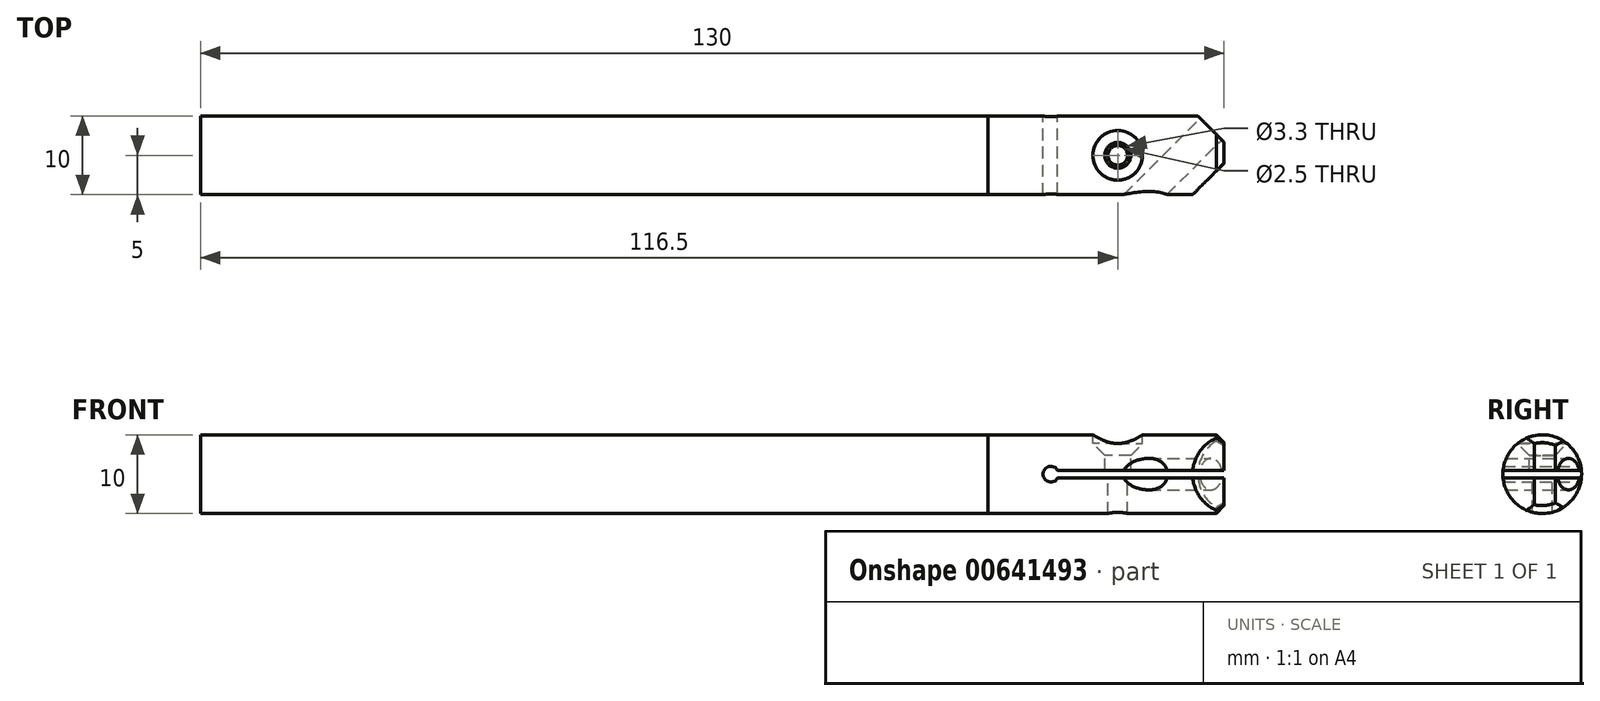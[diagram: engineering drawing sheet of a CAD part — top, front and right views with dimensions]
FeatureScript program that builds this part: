
annotation { "Feature Type Name" : "Feature", "Feature Type Description" : "" }
export const myFeature = defineFeature(function(context is Context, id is Id, definition is map)
    precondition{}
    {
        {
            var Q0;
            Q0=qCreatedBy(makeId("Right.planeOp"),FACE);
            var sketch = newSketch(context, id + "F0", { "sketchPlane" : qUnion([Q0])});
            skCircle(sketch, "E0", {"center": v(0, 0) * mm, "radius": 5 * mm});
            skSolve(sketch);
        }
        {
            var Q0;
            Q0=makeQuery(id+"F0.imprint","IMPRINT",FACE,{"disambiguationData":[TD([[makeQuery(id+"F0.imprint","IMPRINT",EDGE,{"derivedFrom":sQuery(id+"F0.wireOp",EDGE,"E0")}),1.0]])]});
            extrude(context, id + "F1", {"entities" : qUnion([Q0]), "endBound" : BoundingType.SYMMETRIC, "depth" : 100 * mm, "offsetDistance" : 25 * mm});
        }
        {
            var Q0;
            Q0=makeQuery(id+"F1.opExtrude","CAP_FACE",FACE,{"disambiguationData":[OSD([sQuery(id+"F0.wireOp",EDGE,"E0")])],"isStart":false});
            var sketch = newSketch(context, id + "F2", { "sketchPlane" : qUnion([Q0])});
            skCircle(sketch, "E1.0", {"center": v(0, 0) * mm, "radius": 5 * mm});
            skSolve(sketch);
        }
        {
            var Q0;
            Q0=makeQuery(id+"F2.imprint","IMPRINT",FACE,{"disambiguationData":[TD([[makeQuery(id+"F2.imprint","IMPRINT",EDGE,{"derivedFrom":sQuery(id+"F2.wireOp",EDGE,"E1.0")}),1.0]])]});
            extrude(context, id + "F3", {"entities" : qUnion([Q0]), "depth" : 30 * mm, "offsetDistance" : 25 * mm});
        }
        {
            var Q0;
            Q0=makeQuery(id+"F3.opExtrude","CAP_FACE",FACE,{"disambiguationData":[OSD([sQuery(id+"F2.wireOp",EDGE,"E1.0")])],"isStart":false});
            cPlane(context, id + "F4", {"entities" : qUnion([Q0]), "cplaneType" : CPlaneType.OFFSET, "offset" : 0 * mm, "width" : 150 * mm, "height" : 150 * mm});
        }
        {
            var Q0;
            Q0=qCreatedBy(makeId("Front.planeOp"),FACE);
            cPlane(context, id + "F5", {"entities" : qUnion([Q0]), "cplaneType" : CPlaneType.OFFSET, "offset" : 5 * mm, "oppositeDirection" : true, "width" : 150 * mm, "height" : 150 * mm});
        }
        {
            var Q0;
            Q0=qCreatedBy(makeId("Top.planeOp"),FACE);
            var sketch = newSketch(context, id + "F6", { "sketchPlane" : qUnion([Q0])});
            skLineSegment(sketch, "E2", {"start": v(50, 5) * mm, "end": v(80, 5) * mm});
            skLineSegment(sketch, "E3", {"start": v(80, -5) * mm, "end": v(50, -5) * mm});
            skLineSegment(sketch, "E4", {"start": v(80, 5) * mm, "end": v(68.77, 16.23) * mm});
            skSolve(sketch);
        }
        {
            var Q0;
            Q0=sQuery(id+"F6.wireOp",EDGE,"E4");
            var Q1;
            Q1=qCreatedBy(makeId("Top.planeOp"),FACE);
            cPlane(context, id + "F7", {"entities" : qUnion([Q0, Q1]), "cplaneType" : CPlaneType.LINE_ANGLE, "offset" : 25 * mm, "angle" : 90 * degree, "width" : 150 * mm, "height" : 150 * mm});
        }
        {
            var Q0;
            Q0=qCreatedBy(id+"F7.planeOp",FACE);
            var sketch = newSketch(context, id + "F8", { "sketchPlane" : qUnion([Q0])});
            skEllipse(sketch, "E5.0", {"center": v(56.57, 0) * mm, "majorRadius": 5 * mm, "minorRadius": 3.54 * mm, "majorAxis": v(0, -1)});
            skCircle(sketch, "E6", {"center": v(53.03, 0) * mm, "radius": 2 * mm});
            skSolve(sketch);
        }
        {
            var Q0;
            {var subQ0=sQuery(id+"F8.wireOp",EDGE,"E6");var subQ1=sQuery(id+"F8.wireOp",EDGE,"E5.0");var subQ2=makeQuery(id+"F8.imprint","INTERSECT",VERTEX,{"disambiguationData":[OD(0.0)],"derivedFrom":[subQ1,subQ0]});Q0=makeQuery(id+"F8.imprint","IMPRINT",FACE,{"disambiguationData":[TD([[makeQuery(id+"F8.imprint","IMPRINT",EDGE,{"disambiguationData":[TD([[subQ2,1.0]])],"derivedFrom":subQ1}),1.0]])]});}
            var Q1;
            {var subQ0=sQuery(id+"F8.wireOp",EDGE,"E6");var subQ1=sQuery(id+"F8.wireOp",EDGE,"E5.0");var subQ2=makeQuery(id+"F8.imprint","INTERSECT",VERTEX,{"disambiguationData":[OD(0.0)],"derivedFrom":[subQ1,subQ0]});Q1=makeQuery(id+"F8.imprint","IMPRINT",FACE,{"disambiguationData":[TD([[makeQuery(id+"F8.imprint","IMPRINT",EDGE,{"disambiguationData":[TD([[subQ2,1.0]])],"derivedFrom":subQ1}),-1.0]])]});}
            extrude(context, id + "F9", {"entities" : qUnion([Q0, Q1]), "operationType" : NewBodyOperationType.REMOVE, "endBound" : BoundingType.THROUGH_ALL, "depth" : 25 * mm, "offsetDistance" : 25 * mm});
        }
        {
            var Q0;
            Q0=qCreatedBy(id+"F4.planeOp",FACE);
            var sketch = newSketch(context, id + "F10", { "sketchPlane" : qUnion([Q0])});
            skArc(sketch, "E7.0", {"start": v(4.6, 1.98) * mm, "mid": v(-5, 0) * mm, "end": v(4.6, -1.98) * mm});
            skLineSegment(sketch, "E8", {"start": v(0, 5) * mm, "end": v(9.18, 5) * mm});
            skSolve(sketch);
        }
        {
            var Q0;
            Q0=sQuery(id+"F10.wireOp",EDGE,"E8");
            var Q1;
            Q1=qCreatedBy(makeId("Top.planeOp"),FACE);
            cPlane(context, id + "F11", {"entities" : qUnion([Q0, Q1]), "cplaneType" : CPlaneType.LINE_ANGLE, "offset" : 25 * mm, "angle" : 0 * degree, "width" : 150 * mm, "height" : 150 * mm});
        }
        {
            var Q0;
            Q0=qCreatedBy(id+"F11.planeOp",FACE);
            var sketch = newSketch(context, id + "F12", { "sketchPlane" : qUnion([Q0])});
            skLineSegment(sketch, "E9", {"start": v(75.6, 0) * mm, "end": v(50.14, 0) * mm});
            skCircle(sketch, "E10", {"center": v(66.5, 0) * mm, "radius": 3 * mm});
            skLineSegment(sketch, "E11", {"start": v(50, 5) * mm, "end": v(80, 5) * mm});
            skLineSegment(sketch, "E12.0", {"start": v(80, -5) * mm, "end": v(80, 5) * mm});
            skLineSegment(sketch, "E13", {"start": v(76, 5) * mm, "end": v(80, 1) * mm});
            skLineSegment(sketch, "E14.0", {"start": v(50, -5) * mm, "end": v(80, -5) * mm});
            skLineSegment(sketch, "E15", {"start": v(76.68, -5) * mm, "end": v(80, -1.68) * mm});
            skPoint(sketch, "E16.orphan", {"position": v(80, -5) * mm});
            skPoint(sketch, "E17.orphan", {"position": v(80, -4.6) * mm});
            skSolve(sketch);
        }
        {
            var Q0;
            {var subQ3=sQuery(id+"F12.wireOp",EDGE,"E13");Q0=makeQuery(id+"F12.imprint","IMPRINT",FACE,{"disambiguationData":[TD([[makeQuery(id+"F12.imprint","IMPRINT",EDGE,{"derivedFrom":subQ3}),1.0]])]});}
            extrude(context, id + "F13", {"entities" : qUnion([Q0]), "operationType" : NewBodyOperationType.REMOVE, "endBound" : BoundingType.THROUGH_ALL, "depth" : 25 * mm, "offsetDistance" : 25 * mm});
        }
        {
            var Q0;
            Q0=qCreatedBy(id+"F5.planeOp",FACE);
            var sketch = newSketch(context, id + "F14", { "sketchPlane" : qUnion([Q0])});
            skCircle(sketch, "E18", {"center": v(58, 0) * mm, "radius": 1 * mm});
            skLineSegment(sketch, "E19", {"start": v(58.87, 0.5) * mm, "end": v(80, 0.5) * mm});
            skLineSegment(sketch, "E20", {"start": v(80, 0.5) * mm, "end": v(80, -0.5) * mm});
            skLineSegment(sketch, "E21", {"start": v(80, -0.5) * mm, "end": v(58.87, -0.5) * mm});
            skLineSegment(sketch, "E22", {"start": v(80, 0) * mm, "end": v(78.77, 0) * mm});
            skPoint(sketch, "E22.startSnap0", {"position": v(80, 0) * mm});
            skSolve(sketch);
        }
        {
            var Q0;
            {var subQ0=sQuery(id+"F14.wireOp",EDGE,"E18");var subQ1=makeQuery(id+"F14.imprint","INTERSECT",VERTEX,{"derivedFrom":[subQ0,sQuery(id+"F14.wireOp",EDGE,"E19")]});Q0=makeQuery(id+"F14.imprint","IMPRINT",FACE,{"disambiguationData":[TD([[makeQuery(id+"F14.imprint","IMPRINT",EDGE,{"disambiguationData":[TD([[subQ1,-1.0]])],"derivedFrom":subQ0}),1.0]])]});}
            var Q1;
            {var subQ3=sQuery(id+"F14.wireOp",EDGE,"E19");Q1=makeQuery(id+"F14.imprint","IMPRINT",FACE,{"disambiguationData":[TD([[makeQuery(id+"F14.imprint","IMPRINT",EDGE,{"derivedFrom":subQ3}),-1.0]])]});}
            extrude(context, id + "F15", {"entities" : qUnion([Q0, Q1]), "operationType" : NewBodyOperationType.REMOVE, "endBound" : BoundingType.THROUGH_ALL, "depth" : 25 * mm, "offsetDistance" : 25 * mm});
        }
        {
            var Q0;
            Q0=sQuery(id+"F12.wireOp",VERTEX,"E10.center");
            var Q1;
            Q1=makeQuery(id+"F3.opExtrude","SWEPT_BODY",BODY,{"disambiguationData":[OSD([sQuery(id+"F2.wireOp",EDGE,"E1.0")])]});
            hole(context, id + "F16", {"style" : HoleStyle.C_SINK, "endStyle" : HoleEndStyle.BLIND, "oppositeDirection" : true, "standardTappedOrClearance" : lookupTablePath({ "standard" : "ISO", "size" : "3.3", "type" : "Drilled" }), "standardBlindInLast" : lookupTablePath({ "standard" : "ISO", "size" : "3.3", "type" : "Drilled" }), "holeDiameter" : 3.3 * mm, "cSinkDiameter" : 6.3 * mm, "cSinkAngle" : 90 * degree, "majorDiameter" : 3 * mm, "holeDepth" : 4 * mm, "tappedDepth" : 5.5 * mm, "tapClearance" : 3, "locations" : qUnion([Q0]), "scope" : qUnion([Q1])});
        }
        {
            var Q0;
            Q0=sQuery(id+"F12.wireOp",VERTEX,"E10.center");
            var Q1;
            Q1=makeQuery(id+"F3.opExtrude","SWEPT_BODY",BODY,{"disambiguationData":[OSD([sQuery(id+"F2.wireOp",EDGE,"E1.0")])]});
            hole(context, id + "F17", {"style" : HoleStyle.SIMPLE, "endStyle" : HoleEndStyle.THROUGH, "oppositeDirection" : true, "standardTappedOrClearance" : lookupTablePath({ "standard" : "ISO", "engagement" : "75%", "pitch" : "0.5 mm", "size" : "M3", "type" : "Tapped" }), "standardBlindInLast" : lookupTablePath({ "standard" : "ISO", "engagement" : "75%", "pitch" : "0.5 mm", "size" : "M3", "type" : "Tapped" }), "holeDiameter" : 2.5 * mm, "majorDiameter" : 3 * mm, "showTappedDepth" : true, "tappedDepth" : 5.5 * mm, "tapClearance" : 3, "locations" : qUnion([Q0]), "scope" : qUnion([Q1])});
        }
        {
            var Q0;
            {var subQ3=sQuery(id+"F12.wireOp",EDGE,"E15");Q0=makeQuery(id+"F12.imprint","IMPRINT",FACE,{"disambiguationData":[TD([[makeQuery(id+"F12.imprint","IMPRINT",EDGE,{"derivedFrom":subQ3}),-1.0]])]});}
            extrude(context, id + "F18", {"entities" : qUnion([Q0]), "operationType" : NewBodyOperationType.REMOVE, "endBound" : BoundingType.THROUGH_ALL, "depth" : 25 * mm, "offsetDistance" : 25 * mm});
        }
        {
            var Q0;
            Q0=makeQuery(id+"F13.boolean.opBoolean","SPLIT",EDGE,{"disambiguationData":[OD(1.0)],"derivedFrom":makeQuery(id+"F3.opExtrude","CAP_EDGE",EDGE,{"disambiguationData":[OSD([sQuery(id+"F2.wireOp",EDGE,"E1.0")])],"isStart":false})});
            var Q1;
            Q1=makeQuery(id+"F13.boolean.opBoolean","SPLIT",EDGE,{"disambiguationData":[OD(0.0)],"derivedFrom":makeQuery(id+"F3.opExtrude","CAP_EDGE",EDGE,{"disambiguationData":[OSD([sQuery(id+"F2.wireOp",EDGE,"E1.0")])],"isStart":false})});
            chamfer(context, id + "F19", {"entities" : qUnion([Q0, Q1]), "width" : 1 * mm, "tangentPropagation" : true});
        }
    });
